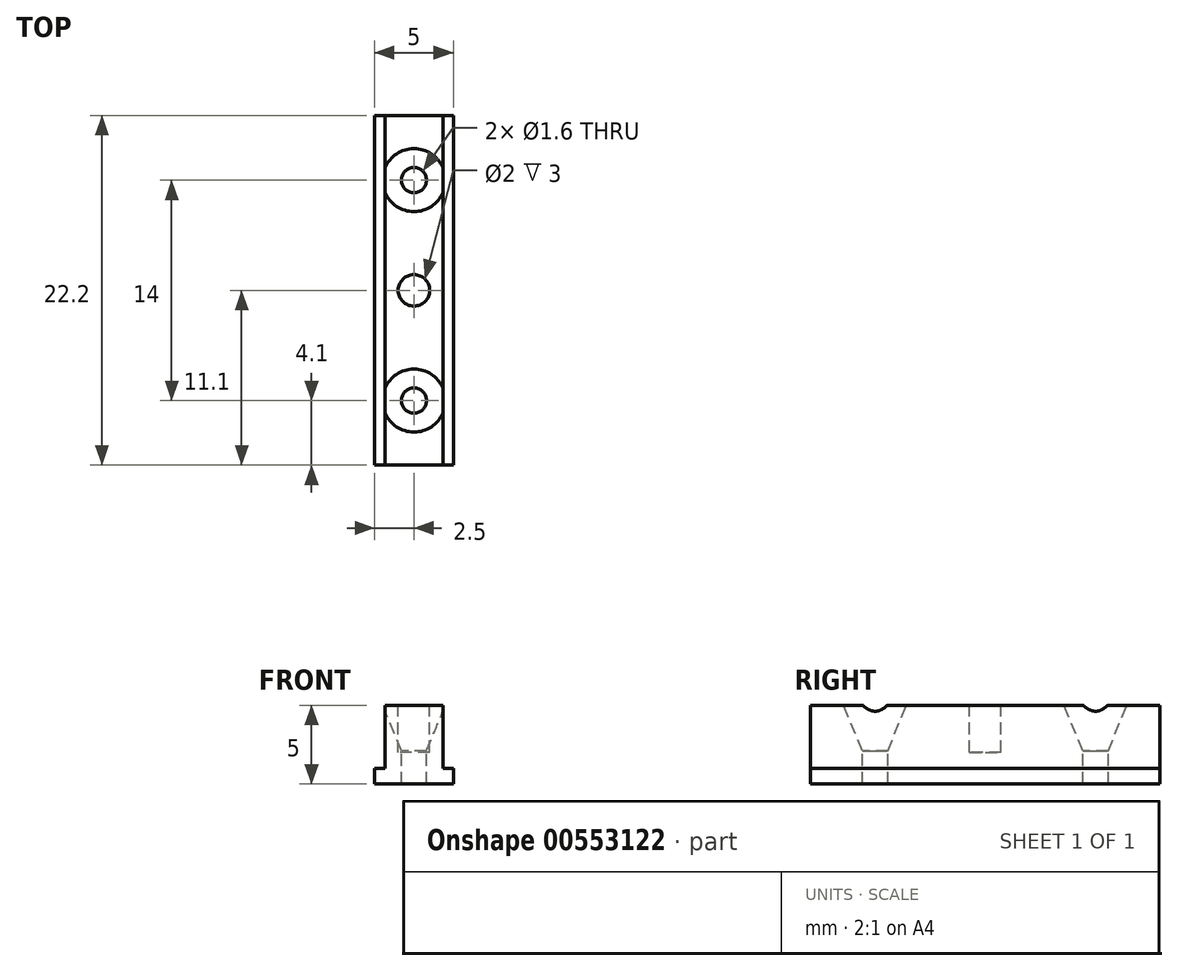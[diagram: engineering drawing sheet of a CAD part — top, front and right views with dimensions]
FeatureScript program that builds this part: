
annotation { "Feature Type Name" : "Feature", "Feature Type Description" : "" }
export const myFeature = defineFeature(function(context is Context, id is Id, definition is map)
    precondition{}
    {
        {
            var Q0;
            Q0=qCreatedBy(makeId("Front.planeOp"),FACE);
            var sketch = newSketch(context, id + "F0", { "sketchPlane" : qUnion([Q0])});
            skLineSegment(sketch, "E0", {"start": v(-2.5, 0) * mm, "end": v(2.5, 0) * mm});
            skLineSegment(sketch, "E1", {"start": v(2.5, 0) * mm, "end": v(2.5, 1) * mm});
            skLineSegment(sketch, "E2", {"start": v(2.5, 1) * mm, "end": v(1.84, 1) * mm});
            skLineSegment(sketch, "E3", {"start": v(1.84, 1) * mm, "end": v(1.84, 5) * mm});
            skLineSegment(sketch, "E4", {"start": v(1.84, 5) * mm, "end": v(-1.84, 5) * mm});
            skLineSegment(sketch, "E5", {"start": v(-1.84, 5) * mm, "end": v(-1.84, 1) * mm});
            skLineSegment(sketch, "E6", {"start": v(-1.84, 1) * mm, "end": v(-2.5, 1) * mm});
            skLineSegment(sketch, "E7", {"start": v(-2.5, 1) * mm, "end": v(-2.5, 0) * mm});
            skSolve(sketch);
        }
        {
            var Q0;
            Q0 = qSketchRegion(id + "F0", true);
            extrude(context, id + "F1", {"entities" : qUnion([Q0]), "endBound" : BoundingType.SYMMETRIC, "depth" : 22.2 * mm, "offsetDistance" : 25 * mm});
        }
        {
            var Q0;
            Q0=makeQuery(id+"F1.opExtrude","SWEPT_FACE",FACE,{"disambiguationData":[OSD([sQuery(id+"F0.wireOp",EDGE,"E4")])]});
            var sketch = newSketch(context, id + "F2", { "sketchPlane" : qUnion([Q0])});
            skCircle(sketch, "E8", {"center": v(0, 0) * mm, "radius": 1 * mm});
            skSolve(sketch);
        }
        {
            var Q0;
            {var subQ1=sQuery(id+"F0.wireOp",EDGE,"E5");var subQ2=sQuery(id+"F0.wireOp",EDGE,"E4");var subQ3=sQuery(id+"F0.wireOp",EDGE,"E3");Q0=makeQuery(id+"FTHiFEOFWEqODZF_1.boolean.opBoolean","SPLIT",FACE,{"disambiguationData":[TD([makeQuery(id+"F1.opExtrude","CAP_FACE",FACE,{"disambiguationData":[OSD([sQuery(id+"F0.wireOp",EDGE,"E0"),sQuery(id+"F0.wireOp",EDGE,"E1"),sQuery(id+"F0.wireOp",EDGE,"E2"),subQ3,subQ2,subQ1,sQuery(id+"F0.wireOp",EDGE,"E6"),sQuery(id+"F0.wireOp",EDGE,"E7")])],"isStart":true})])],"derivedFrom":makeQuery(id+"F1.opExtrude","SWEPT_FACE",FACE,{"disambiguationData":[OSD([subQ2])]})});}
            var sketch = newSketch(context, id + "F3", { "sketchPlane" : qUnion([Q0])});
            skPoint(sketch, "E9", {"position": v(0, 7) * mm});
            skPoint(sketch, "E10", {"position": v(0, -7) * mm});
            skSolve(sketch);
        }
        {
            var Q0;
            Q0=sQuery(id+"F3.wireOp",VERTEX,"E9");
            var Q1;
            Q1=sQuery(id+"F3.wireOp",VERTEX,"E10");
            var Q2;
            Q2=makeQuery(id+"F1.opExtrude","SWEPT_BODY",BODY,{"disambiguationData":[OSD([sQuery(id+"F0.wireOp",EDGE,"E0"),sQuery(id+"F0.wireOp",EDGE,"E1"),sQuery(id+"F0.wireOp",EDGE,"E2"),sQuery(id+"F0.wireOp",EDGE,"E3"),sQuery(id+"F0.wireOp",EDGE,"E4"),sQuery(id+"F0.wireOp",EDGE,"E5"),sQuery(id+"F0.wireOp",EDGE,"E6"),sQuery(id+"F0.wireOp",EDGE,"E7")])]});
            hole(context, id + "F4", {"style" : HoleStyle.C_SINK, "endStyle" : HoleEndStyle.THROUGH, "holeDiameter" : 1.6 * mm, "cSinkDiameter" : 4 * mm, "cSinkAngle" : 45 * degree, "isTappedThrough" : true, "tappedDepth" : 12 * mm, "tapClearance" : 3, "startFromSketch" : true, "locations" : qUnion([Q0, Q1]), "scope" : qUnion([Q2])});
        }
        {
            var Q0;
            Q0=makeQuery(id+"F2.imprint","IMPRINT",FACE,{"disambiguationData":[TD([[makeQuery(id+"F2.imprint","IMPRINT",EDGE,{"derivedFrom":sQuery(id+"F2.wireOp",EDGE,"E8")}),-1.0]])]});
            var sketch = newSketch(context, id + "F5", { "sketchPlane" : qUnion([Q0])});
            skCircle(sketch, "E11", {"center": v(0, 0) * mm, "radius": 1 * mm});
            skSolve(sketch);
        }
        {
            var Q0;
            Q0 = qSketchRegion(id + "F5", true);
            extrude(context, id + "F6", {"entities" : qUnion([Q0]), "operationType" : NewBodyOperationType.REMOVE, "oppositeDirection" : true, "depth" : 3 * mm, "offsetDistance" : 25 * mm});
        }
    });
